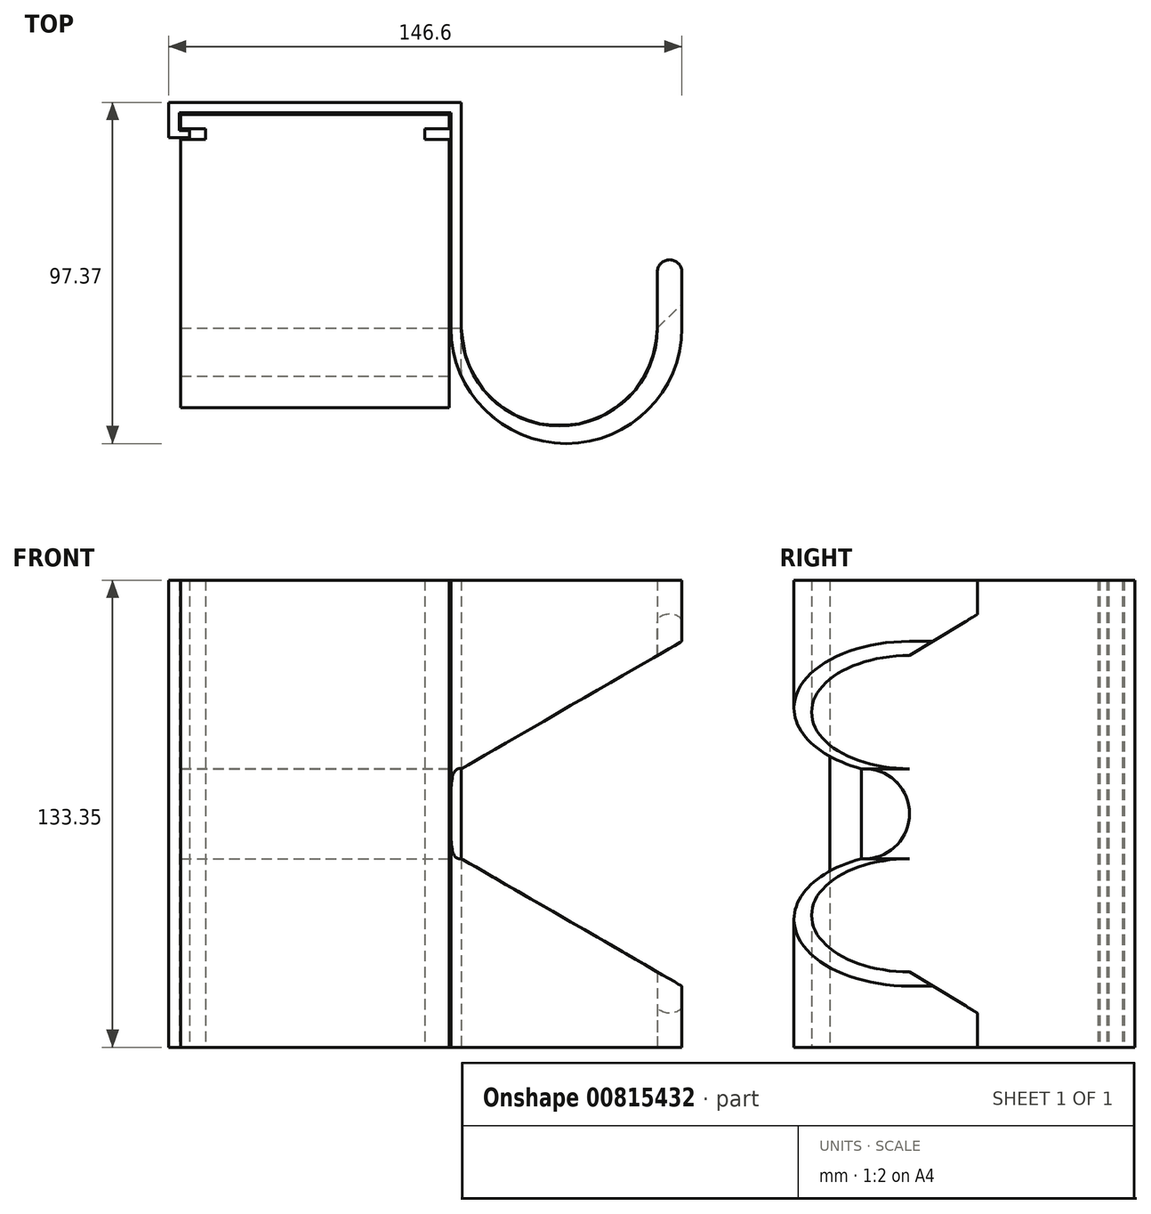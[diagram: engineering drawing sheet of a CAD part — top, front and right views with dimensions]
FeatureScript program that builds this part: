
annotation { "Feature Type Name" : "Feature", "Feature Type Description" : "" }
export const myFeature = defineFeature(function(context is Context, id is Id, definition is map)
    precondition{}
    {
        {
            assignVariable(context, id + "F0", {"name" : "hanger", "anyValue" : 5.25 * 25.4});
        }
        {
            var Q0;
            Q0=qCreatedBy(makeId("Top.planeOp"),FACE);
            var sketch = newSketch(context, id + "F1", { "sketchPlane" : qUnion([Q0])});
            skLineSegment(sketch, "E0.top", {"start": v(38.3, 2) * mm, "end": v(-38.3, 2) * mm});
            skLineSegment(sketch, "E0.left", {"start": v(38.3, -2) * mm, "end": v(38.3, 2) * mm});
            skLineSegment(sketch, "E0.right", {"start": v(-38.3, -2) * mm, "end": v(-38.3, 2) * mm});
            skPoint(sketch, "E0.middle", {"position": v(0, 0) * mm});
            skLineSegment(sketch, "E1.left", {"start": v(-31.3, -2) * mm, "end": v(-31.3, -5) * mm});
            skLineSegment(sketch, "E1.right", {"start": v(31.3, -2) * mm, "end": v(31.3, -5) * mm});
            skLineSegment(sketch, "E2", {"start": v(-38.3, -2) * mm, "end": v(-31.3, -2) * mm});
            skLineSegment(sketch, "E3", {"start": v(31.3, -2) * mm, "end": v(38.3, -2) * mm});
            skLineSegment(sketch, "E4.bottom", {"start": v(-38.3, -5) * mm, "end": v(-31.3, -5) * mm});
            skLineSegment(sketch, "E4.top", {"start": v(-38.3, -81.6) * mm, "end": v(38.3, -81.6) * mm});
            skLineSegment(sketch, "E4.left", {"start": v(-38.3, -5) * mm, "end": v(-38.3, -81.6) * mm});
            skLineSegment(sketch, "E4.right", {"start": v(38.3, -5) * mm, "end": v(38.3, -81.6) * mm});
            skLineSegment(sketch, "E5.trimOffspring", {"start": v(31.3, -5) * mm, "end": v(38.3, -5) * mm});
            skSolve(sketch);
        }
        {
            var Q0;
            Q0=qCreatedBy(makeId("Top.planeOp"),FACE);
            var sketch = newSketch(context, id + "F2", { "sketchPlane" : qUnion([Q0])});
            skLineSegment(sketch, "E6", {"start": v(-35.8, -4.5) * mm, "end": v(-41.8, -4.5) * mm});
            skLineSegment(sketch, "E7", {"start": v(-41.8, -4.5) * mm, "end": v(-41.8, 5.5) * mm});
            skLineSegment(sketch, "E8", {"start": v(-41.8, 5.5) * mm, "end": v(41.8, 5.5) * mm});
            skLineSegment(sketch, "E9", {"start": v(38.8, -58.87) * mm, "end": v(38.8, 2.5) * mm});
            skLineSegment(sketch, "E10", {"start": v(38.8, 2.5) * mm, "end": v(-38.8, 2.5) * mm});
            skLineSegment(sketch, "E11", {"start": v(-38.8, 2.5) * mm, "end": v(-38.8, -2.5) * mm});
            skLineSegment(sketch, "E12", {"start": v(-38.8, -2.5) * mm, "end": v(-38.8, -2.5) * mm});
            skLineSegment(sketch, "E13", {"start": v(41.8, 5.5) * mm, "end": v(41.8, -58.87) * mm});
            skLineSegment(sketch, "E14", {"start": v(41.8, -58.87) * mm, "end": v(97.8, -58.87) * mm, "construction": true});
            skLineSegment(sketch, "E15", {"start": v(97.8, -58.87) * mm, "end": v(97.8, -42.9) * mm});
            skLineSegment(sketch, "E16", {"start": v(97.8, -42.9) * mm, "end": v(104.8, -42.9) * mm, "construction": true});
            skLineSegment(sketch, "E17", {"start": v(104.8, -42.9) * mm, "end": v(104.8, -58.87) * mm});
            skLineSegment(sketch, "E18", {"start": v(104.8, -58.87) * mm, "end": v(38.8, -58.87) * mm, "construction": true});
            skArc(sketch, "E19", {"start": v(41.8, -58.87) * mm, "mid": v(69.8, -86.87) * mm, "end": v(97.8, -58.87) * mm});
            skArc(sketch, "E20", {"start": v(38.8, -58.87) * mm, "mid": v(71.8, -91.87) * mm, "end": v(104.8, -58.87) * mm});
            skArc(sketch, "E21", {"start": v(104.8, -42.9) * mm, "mid": v(101.3, -39.4) * mm, "end": v(97.8, -42.9) * mm});
            skLineSegment(sketch, "E22", {"start": v(-38.8, -2.5) * mm, "end": v(-35.8, -2.5) * mm});
            skLineSegment(sketch, "E23", {"start": v(-35.8, -2.5) * mm, "end": v(-35.8, -4.5) * mm});
            skSolve(sketch);
        }
        {
            var Q0;
            Q0 = qSketchRegion(id + "F1", true);
            var Q1;
            Q1=makeQuery(id+"F2.imprint","IMPRINT",FACE,{"disambiguationData":[TD([[makeQuery(id+"F2.imprint","IMPRINT",EDGE,{"derivedFrom":sQuery(id+"F2.wireOp",EDGE,"E6")}),-1.0]])]});
            extrude(context, id + "F3", {"entities" : qUnion([Q0, Q1]), "depth" : (getVariable(context, 'hanger')) * mm, "offsetDistance" : 25 * mm});
        }
        {
            var Q0;
            Q0=makeQuery(id+"F3.opExtrude","SWEPT_FACE",FACE,{"disambiguationData":[OSD([sQuery(id+"F2.wireOp",EDGE,"E8")])]});
            var sketch = newSketch(context, id + "F4", { "sketchPlane" : qUnion([Q0])});
            skPoint(sketch, "E24.0", {"position": v(-104.8, 17.46) * mm});
            skPoint(sketch, "E25.0", {"position": v(-104.8, 115.89) * mm});
            skPoint(sketch, "E26.0", {"position": v(-41.8, 66.67) * mm});
            skLineSegment(sketch, "E27", {"start": v(-104.8, 115.89) * mm, "end": v(-104.8, 17.46) * mm});
            skLineSegment(sketch, "E28", {"start": v(-41.8, 53.84) * mm, "end": v(-41.8, 79.51) * mm});
            skLineSegment(sketch, "E29", {"start": v(-104.8, 17.46) * mm, "end": v(-41.8, 53.84) * mm});
            skLineSegment(sketch, "E30", {"start": v(-41.8, 79.51) * mm, "end": v(-104.8, 115.89) * mm});
            skLineSegment(sketch, "E31.0", {"start": v(-104.8, 133.35) * mm, "end": v(-104.8, 0) * mm, "construction": true});
            skLineSegment(sketch, "E32.0", {"start": v(-41.8, 133.35) * mm, "end": v(-41.8, 0) * mm, "construction": true});
            skSolve(sketch);
        }
        {
            var Q0;
            Q0 = qSketchRegion(id + "F4", true);
            extrude(context, id + "F5", {"entities" : qUnion([Q0]), "operationType" : NewBodyOperationType.REMOVE, "endBound" : BoundingType.THROUGH_ALL, "oppositeDirection" : true, "depth" : 25 * mm, "offsetDistance" : 25 * mm});
        }
        {
            var Q0;
            Q0=makeQuery(id+"F5.boolean.opBoolean","MERGE",FACE,{"derivedFrom":[makeQuery(id+"F3.opExtrude","SWEPT_FACE",FACE,{"disambiguationData":[OSD([sQuery(id+"F2.wireOp",EDGE,"E13")])]}),makeQuery(id+"F5.opExtrude","SWEPT_FACE",FACE,{"disambiguationData":[OSD([sQuery(id+"F4.wireOp",EDGE,"E28")])]})]});
            var sketch = newSketch(context, id + "F6", { "sketchPlane" : qUnion([Q0])});
            skArc(sketch, "E33", {"start": v(-72.62, 53.84) * mm, "mid": v(-58.87, 66.67) * mm, "end": v(-72.62, 79.51) * mm});
            skLineSegment(sketch, "E34", {"start": v(-58.87, 79.51) * mm, "end": v(-58.87, 66.67) * mm, "construction": true});
            skPoint(sketch, "E34.endSnap0", {"position": v(-58.87, 66.67) * mm});
            skLineSegment(sketch, "E35", {"start": v(-72.62, 79.51) * mm, "end": v(-72.62, 53.84) * mm});
            skSolve(sketch);
        }
        {
            var Q0;
            Q0 = qSketchRegion(id + "F6", true);
            extrude(context, id + "F7", {"entities" : qUnion([Q0]), "operationType" : NewBodyOperationType.REMOVE, "endBound" : BoundingType.THROUGH_ALL, "oppositeDirection" : true, "depth" : 25 * mm, "offsetDistance" : 25 * mm});
        }
        {
            var Q0;
            {var subQ2=sQuery(id+"F2.wireOp",EDGE,"E17");Q0=makeQuery(id+"F5.boolean.opBoolean","SPLIT",FACE,{"disambiguationData":[TD([makeQuery(id+"F5.opExtrude","SWEPT_FACE",FACE,{"disambiguationData":[OSD([sQuery(id+"F4.wireOp",EDGE,"E30")])]})])],"derivedFrom":makeQuery(id+"F3.opExtrude","SWEPT_FACE",FACE,{"disambiguationData":[OSD([subQ2])]})});}
            var sketch = newSketch(context, id + "F8", { "sketchPlane" : qUnion([Q0])});
            skPoint(sketch, "E36.0", {"position": v(-58.87, 111.85) * mm});
            skLineSegment(sketch, "E37", {"start": v(-39.4, 133.35) * mm, "end": v(-39.4, 113.87) * mm});
            skLineSegment(sketch, "E38", {"start": v(-39.4, 123.6) * mm, "end": v(-58.87, 111.85) * mm});
            skLineSegment(sketch, "E39", {"start": v(-58.87, 111.85) * mm, "end": v(-39.4, 111.85) * mm});
            skLineSegment(sketch, "E40", {"start": v(-39.4, 111.85) * mm, "end": v(-39.4, 113.87) * mm});
            skPoint(sketch, "E41.0", {"position": v(5.5, 66.67) * mm});
            skLineSegment(sketch, "E42", {"start": v(5.5, 66.67) * mm, "end": v(-22.06, 66.67) * mm, "construction": true});
            skLineSegment(sketch, "E43.MirrorCS", {"start": v(-39.4, 9.74) * mm, "end": v(-58.87, 21.5) * mm});
            skLineSegment(sketch, "E44.MirrorCS", {"start": v(-39.4, 0) * mm, "end": v(-39.4, 19.48) * mm});
            skLineSegment(sketch, "E45.MirrorCS", {"start": v(-39.4, 21.5) * mm, "end": v(-39.4, 19.48) * mm});
            skLineSegment(sketch, "E46.MirrorCS", {"start": v(-58.87, 21.5) * mm, "end": v(-39.4, 21.5) * mm});
            skSolve(sketch);
        }
        {
            var Q0;
            Q0 = qSketchRegion(id + "F8", true);
            var Q1;
            Q1=makeQuery(id+"F5.boolean.opBoolean","MERGE",FACE,{"derivedFrom":[makeQuery(id+"F3.opExtrude","SWEPT_FACE",FACE,{"disambiguationData":[OSD([sQuery(id+"F2.wireOp",EDGE,"E13")])]}),makeQuery(id+"F5.opExtrude","SWEPT_FACE",FACE,{"disambiguationData":[OSD([sQuery(id+"F4.wireOp",EDGE,"E28")])]})]});
            extrude(context, id + "F9", {"entities" : qUnion([Q0]), "operationType" : NewBodyOperationType.REMOVE, "endBound" : BoundingType.UP_TO_SURFACE, "oppositeDirection" : true, "depth" : 25 * mm, "endBoundEntityFace" : qUnion([Q1]), "offsetDistance" : 25 * mm});
        }
    });
